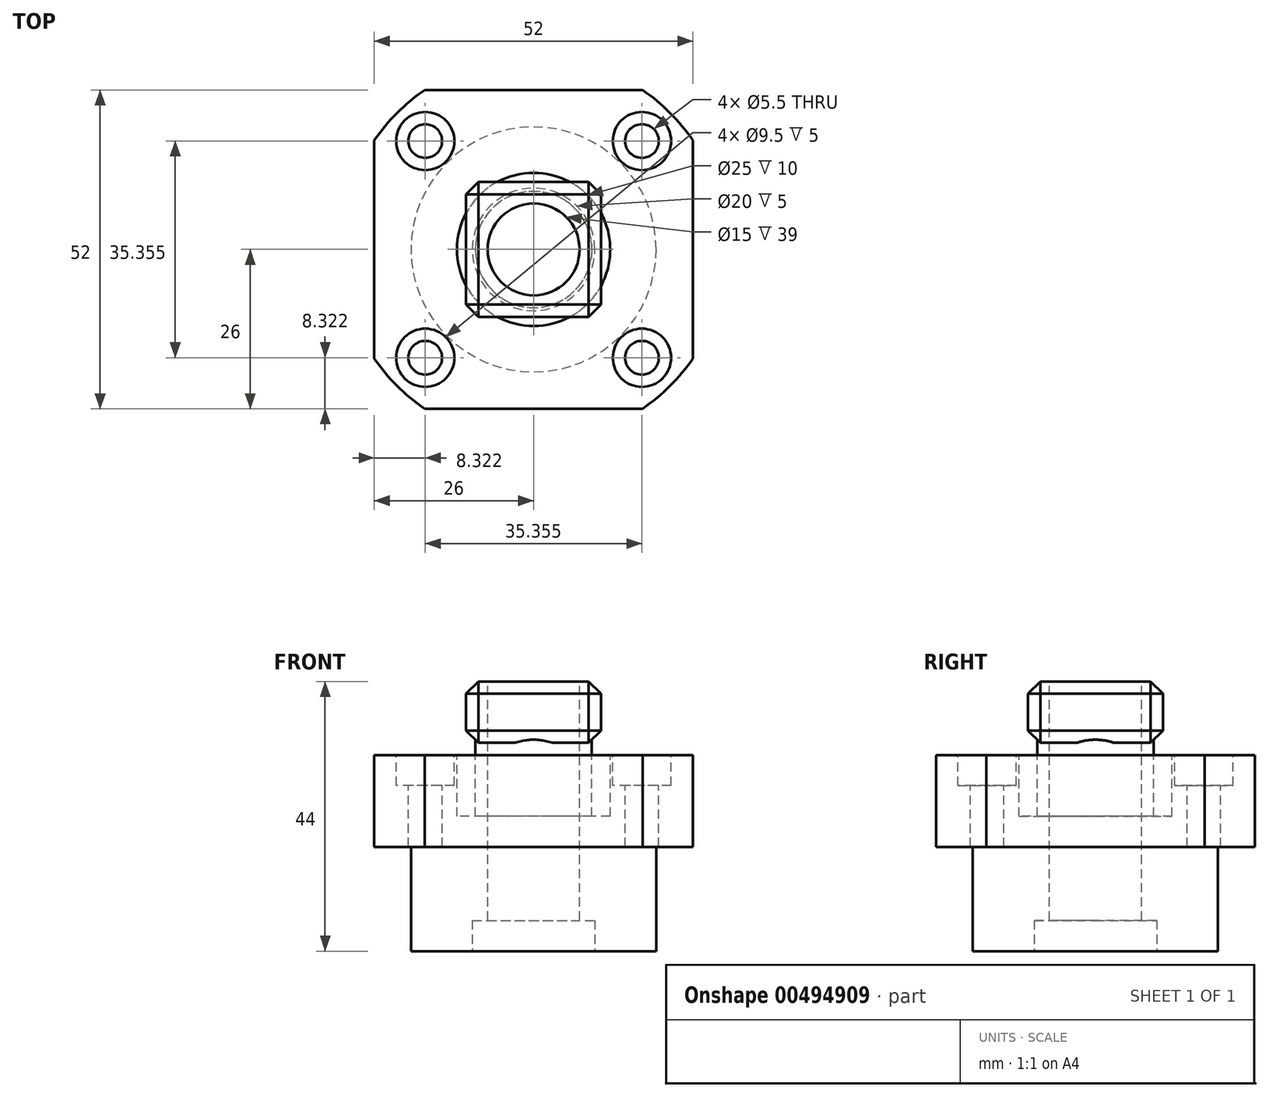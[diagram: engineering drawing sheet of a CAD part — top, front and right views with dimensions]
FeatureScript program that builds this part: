
annotation { "Feature Type Name" : "Feature", "Feature Type Description" : "" }
export const myFeature = defineFeature(function(context is Context, id is Id, definition is map)
    precondition{}
    {
        {
            var Q0;
            Q0=qCreatedBy(makeId("Top.planeOp"),FACE);
            var sketch = newSketch(context, id + "F0", { "sketchPlane" : qUnion([Q0])});
            skCircle(sketch, "E0", {"center": v(0, 0) * mm, "radius": 20 * mm});
            skSolve(sketch);
        }
        {
            var Q0;
            Q0=qSketchRegion(id+"F0",true);
            extrude(context, id + "F1", {"entities" : qUnion([Q0]), "oppositeDirection" : true, "depth" : 17 * mm});
        }
        {
            var Q0;
            Q0=qCreatedBy(makeId("Top.planeOp"),FACE);
            var sketch = newSketch(context, id + "F2", { "sketchPlane" : qUnion([Q0])});
            skLineSegment(sketch, "E1.bottom", {"start": v(-17.78, 26) * mm, "end": v(17.78, 26) * mm});
            skLineSegment(sketch, "E1.top", {"start": v(-17.78, -26) * mm, "end": v(17.78, -26) * mm});
            skLineSegment(sketch, "E1.left", {"start": v(-26, 17.78) * mm, "end": v(-26, -17.78) * mm});
            skLineSegment(sketch, "E1.right", {"start": v(26, 17.78) * mm, "end": v(26, -17.78) * mm});
            skArc(sketch, "E2", {"start": v(-26, -17.78) * mm, "mid": v(-22.27, -22.27) * mm, "end": v(-17.78, -26) * mm});
            skArc(sketch, "E3.trimOffspring", {"start": v(17.78, -26) * mm, "mid": v(22.27, -22.27) * mm, "end": v(26, -17.78) * mm});
            skArc(sketch, "E4.trimOffspring", {"start": v(26, 17.78) * mm, "mid": v(22.27, 22.27) * mm, "end": v(17.78, 26) * mm});
            skArc(sketch, "E5.trimOffspring", {"start": v(-17.78, 26) * mm, "mid": v(-22.27, 22.27) * mm, "end": v(-26, 17.78) * mm});
            skSolve(sketch);
        }
        {
            var Q0;
            Q0=qSketchRegion(id+"F2",true);
            extrude(context, id + "F3", {"entities" : qUnion([Q0]), "operationType" : NewBodyOperationType.ADD, "depth" : 15 * mm});
        }
        {
            var Q0;
            Q0=makeQuery(id+"F3.opExtrude","CAP_FACE",FACE,{"disambiguationData":[OSD([sQuery(id+"F2.wireOp",EDGE,"E1.bottom"),sQuery(id+"F2.wireOp",EDGE,"E1.top"),sQuery(id+"F2.wireOp",EDGE,"E1.left"),sQuery(id+"F2.wireOp",EDGE,"E1.right"),sQuery(id+"F2.wireOp",EDGE,"E2"),sQuery(id+"F2.wireOp",EDGE,"E3.trimOffspring"),sQuery(id+"F2.wireOp",EDGE,"E4.trimOffspring"),sQuery(id+"F2.wireOp",EDGE,"E5.trimOffspring")])],"isStart":false});
            var sketch = newSketch(context, id + "F4", { "sketchPlane" : qUnion([Q0])});
            skCircle(sketch, "E6", {"center": v(0, 0) * mm, "radius": 12.5 * mm});
            skCircle(sketch, "E7", {"center": v(0, 0) * mm, "radius": 9.5 * mm});
            skSolve(sketch);
        }
        {
            var Q0;
            Q0=qSketchRegion(id+"F4",true);
            extrude(context, id + "F5", {"entities" : qUnion([Q0]), "operationType" : NewBodyOperationType.REMOVE, "oppositeDirection" : true, "depth" : 10 * mm});
        }
        {
            var Q0;
            Q0=makeQuery(id+"F5.boolean.opBoolean","SPLIT",FACE,{"disambiguationData":[TD([makeQuery(id+"F5.opExtrude","SWEPT_FACE",FACE,{"disambiguationData":[OSD([sQuery(id+"F4.wireOp",EDGE,"E7")])]})])],"derivedFrom":makeQuery(id+"F3.opExtrude","CAP_FACE",FACE,{"disambiguationData":[OSD([sQuery(id+"F2.wireOp",EDGE,"E1.bottom"),sQuery(id+"F2.wireOp",EDGE,"E1.top"),sQuery(id+"F2.wireOp",EDGE,"E1.left"),sQuery(id+"F2.wireOp",EDGE,"E1.right"),sQuery(id+"F2.wireOp",EDGE,"E2"),sQuery(id+"F2.wireOp",EDGE,"E3.trimOffspring"),sQuery(id+"F2.wireOp",EDGE,"E4.trimOffspring"),sQuery(id+"F2.wireOp",EDGE,"E5.trimOffspring")])],"isStart":false})});
            var sketch = newSketch(context, id + "F6", { "sketchPlane" : qUnion([Q0])});
            skCircle(sketch, "E8", {"center": v(0, 0) * mm, "radius": 9.5 * mm});
            skSolve(sketch);
        }
        {
            var Q0;
            Q0=qSketchRegion(id+"F6",true);
            extrude(context, id + "F7", {"entities" : qUnion([Q0]), "operationType" : NewBodyOperationType.ADD, "depth" : 2 * mm});
        }
        {
            var Q0;
            Q0=makeQuery(id+"F7.opExtrude","CAP_FACE",FACE,{"disambiguationData":[OSD([sQuery(id+"F6.wireOp",EDGE,"E8")])],"isStart":false});
            var sketch = newSketch(context, id + "F8", { "sketchPlane" : qUnion([Q0])});
            skLineSegment(sketch, "E9.bottom", {"start": v(-11, 11) * mm, "end": v(11, 11) * mm});
            skLineSegment(sketch, "E9.top", {"start": v(-11, -11) * mm, "end": v(11, -11) * mm});
            skLineSegment(sketch, "E9.left", {"start": v(-11, 11) * mm, "end": v(-11, -11) * mm});
            skLineSegment(sketch, "E9.right", {"start": v(11, 11) * mm, "end": v(11, -11) * mm});
            skSolve(sketch);
        }
        {
            var Q0;
            Q0=qSketchRegion(id+"F8",true);
            extrude(context, id + "F9", {"entities" : qUnion([Q0]), "operationType" : NewBodyOperationType.ADD, "depth" : 10 * mm});
        }
        {
            var Q0;
            Q0=makeQuery(id+"F9.opExtrude","SWEPT_EDGE",EDGE,{"disambiguationData":[OSD([sQuery(id+"F8.wireOp",EDGE,"E9.bottom"),sQuery(id+"F8.wireOp",EDGE,"E9.left")])]});
            var Q1;
            Q1=makeQuery(id+"F9.opExtrude","SWEPT_EDGE",EDGE,{"disambiguationData":[OSD([sQuery(id+"F8.wireOp",EDGE,"E9.bottom"),sQuery(id+"F8.wireOp",EDGE,"E9.right")])]});
            var Q2;
            Q2=makeQuery(id+"F9.opExtrude","SWEPT_EDGE",EDGE,{"disambiguationData":[OSD([sQuery(id+"F8.wireOp",EDGE,"E9.top"),sQuery(id+"F8.wireOp",EDGE,"E9.right")])]});
            var Q3;
            Q3=makeQuery(id+"F9.opExtrude","SWEPT_EDGE",EDGE,{"disambiguationData":[OSD([sQuery(id+"F8.wireOp",EDGE,"E9.top"),sQuery(id+"F8.wireOp",EDGE,"E9.left")])]});
            var Q4;
            Q4=makeQuery(id+"F9.opExtrude","CAP_EDGE",EDGE,{"disambiguationData":[OSD([sQuery(id+"F8.wireOp",EDGE,"E9.left")])],"isStart":true});
            var Q5;
            Q5=makeQuery(id+"F9.opExtrude","SWEPT_FACE",FACE,{"disambiguationData":[OSD([sQuery(id+"F8.wireOp",EDGE,"E9.left")])]});
            var Q6;
            Q6=makeQuery(id+"F9.opExtrude","CAP_EDGE",EDGE,{"disambiguationData":[OSD([sQuery(id+"F8.wireOp",EDGE,"E9.right")])],"isStart":false});
            var Q7;
            Q7=makeQuery(id+"F9.opExtrude","CAP_EDGE",EDGE,{"disambiguationData":[OSD([sQuery(id+"F8.wireOp",EDGE,"E9.right")])],"isStart":true});
            var Q8;
            Q8=makeQuery(id+"F9.opExtrude","CAP_EDGE",EDGE,{"disambiguationData":[OSD([sQuery(id+"F8.wireOp",EDGE,"E9.top")])],"isStart":false});
            var Q9;
            Q9=makeQuery(id+"F9.opExtrude","SWEPT_FACE",FACE,{"disambiguationData":[OSD([sQuery(id+"F8.wireOp",EDGE,"E9.top")])]});
            var Q10;
            Q10=makeQuery(id+"F9.opExtrude","CAP_EDGE",EDGE,{"disambiguationData":[OSD([sQuery(id+"F8.wireOp",EDGE,"E9.bottom")])],"isStart":false});
            var Q11;
            Q11=makeQuery(id+"F9.opExtrude","CAP_EDGE",EDGE,{"disambiguationData":[OSD([sQuery(id+"F8.wireOp",EDGE,"E9.bottom")])],"isStart":true});
            chamfer(context, id + "F10", {"entities" : qUnion([Q0, Q1, Q2, Q3, Q4, Q5, Q6, Q7, Q8, Q9, Q10, Q11]), "width" : 2 * mm, "tangentPropagation" : true});
        }
        {
            var Q0;
            Q0=makeQuery(id+"F1.opExtrude","CAP_FACE",FACE,{"disambiguationData":[OSD([sQuery(id+"F0.wireOp",EDGE,"E0")])],"isStart":false});
            var sketch = newSketch(context, id + "F11", { "sketchPlane" : qUnion([Q0])});
            skCircle(sketch, "E10", {"center": v(0, 0) * mm, "radius": 10 * mm});
            skSolve(sketch);
        }
        {
            var Q0;
            Q0=qSketchRegion(id+"F11",true);
            extrude(context, id + "F12", {"entities" : qUnion([Q0]), "operationType" : NewBodyOperationType.REMOVE, "oppositeDirection" : true, "depth" : 5 * mm});
        }
        {
            var Q0;
            Q0=makeQuery(id+"F9.opExtrude","CAP_FACE",FACE,{"disambiguationData":[OSD([sQuery(id+"F8.wireOp",EDGE,"E9.bottom"),sQuery(id+"F8.wireOp",EDGE,"E9.top"),sQuery(id+"F8.wireOp",EDGE,"E9.left"),sQuery(id+"F8.wireOp",EDGE,"E9.right")])],"isStart":false});
            var sketch = newSketch(context, id + "F13", { "sketchPlane" : qUnion([Q0])});
            skCircle(sketch, "E11", {"center": v(0, 0) * mm, "radius": 7.5 * mm});
            skSolve(sketch);
        }
        {
            var Q0;
            Q0=qSketchRegion(id+"F13",true);
            extrude(context, id + "F14", {"entities" : qUnion([Q0]), "operationType" : NewBodyOperationType.REMOVE, "endBound" : BoundingType.THROUGH_ALL, "oppositeDirection" : true, "depth" : 25 * mm});
        }
        {
            var Q0;
            Q0=makeQuery(id+"F3.opExtrude","CAP_FACE",FACE,{"disambiguationData":[OSD([sQuery(id+"F2.wireOp",EDGE,"E1.bottom"),sQuery(id+"F2.wireOp",EDGE,"E1.top"),sQuery(id+"F2.wireOp",EDGE,"E1.left"),sQuery(id+"F2.wireOp",EDGE,"E1.right"),sQuery(id+"F2.wireOp",EDGE,"E2"),sQuery(id+"F2.wireOp",EDGE,"E3.trimOffspring"),sQuery(id+"F2.wireOp",EDGE,"E4.trimOffspring"),sQuery(id+"F2.wireOp",EDGE,"E5.trimOffspring")])],"isStart":false});
            var sketch = newSketch(context, id + "F15", { "sketchPlane" : qUnion([Q0])});
            skPoint(sketch, "E12", {"position": v(-17.68, 17.68) * mm});
            skPoint(sketch, "E13", {"position": v(17.68, 17.68) * mm});
            skPoint(sketch, "E14", {"position": v(17.68, -17.68) * mm});
            skPoint(sketch, "E15", {"position": v(-17.68, -17.68) * mm});
            skSolve(sketch);
        }
        {
            var Q0;
            Q0=sQuery(id+"F15.wireOp",VERTEX,"E13");
            var Q1;
            Q1=sQuery(id+"F15.wireOp",VERTEX,"E14");
            var Q2;
            Q2=sQuery(id+"F15.wireOp",VERTEX,"E15");
            var Q3;
            Q3=sQuery(id+"F15.wireOp",VERTEX,"E12");
            var Q4;
            Q4=makeQuery(id+"F1.opExtrude","SWEPT_BODY",BODY,{"disambiguationData":[OSD([sQuery(id+"F0.wireOp",EDGE,"E0")])]});
            hole(context, id + "F16", {"style" : HoleStyle.C_BORE, "endStyle" : HoleEndStyle.THROUGH, "holeDiameter" : 5.5 * mm, "cBoreDiameter" : 9.5 * mm, "cBoreDepth" : 5 * mm, "isTappedThrough" : true, "tappedDepth" : 7.6 * mm, "tapClearance" : 3, "locations" : qUnion([Q0, Q1, Q2, Q3]), "scope" : qUnion([Q4])});
        }
    });
